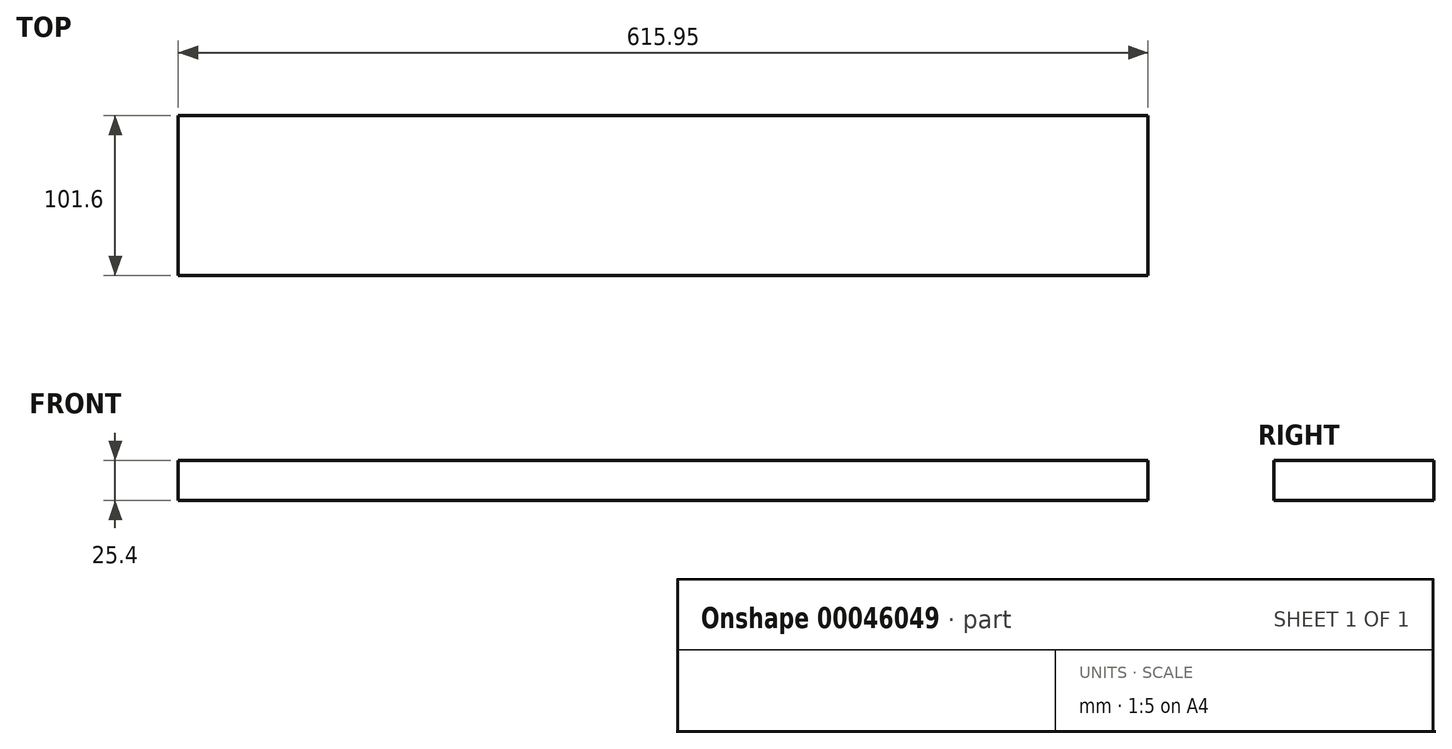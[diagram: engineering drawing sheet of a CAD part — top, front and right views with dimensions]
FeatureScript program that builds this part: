
annotation { "Feature Type Name" : "Feature", "Feature Type Description" : "" }
export const myFeature = defineFeature(function(context is Context, id is Id, definition is map)
    precondition{}
    {
        {
            var Q0;
            Q0=qCreatedBy(makeId("Top.planeOp"),FACE);
            var sketch = newSketch(context, id + "F0", { "sketchPlane" : qUnion([Q0])});
            skLineSegment(sketch, "E0.bottom", {"start": v(0, 0) * mm, "end": v(615.95, 0) * mm});
            skLineSegment(sketch, "E0.top", {"start": v(0, 101.6) * mm, "end": v(615.95, 101.6) * mm});
            skLineSegment(sketch, "E0.left", {"start": v(0, 0) * mm, "end": v(0, 101.6) * mm});
            skLineSegment(sketch, "E0.right", {"start": v(615.95, 0) * mm, "end": v(615.95, 101.6) * mm});
            skSolve(sketch);
        }
        {
            var Q0;
            Q0=makeQuery(id+"F0.imprint","IMPRINT",FACE,{"disambiguationData":[TD([[makeQuery(id+"F0.imprint","IMPRINT",EDGE,{"derivedFrom":sQuery(id+"F0.wireOp",EDGE,"E0.bottom")}),1.0]])]});
            extrude(context, id + "F1", {"entities" : qUnion([Q0]), "depth" : 25.4 * mm});
        }
    });
